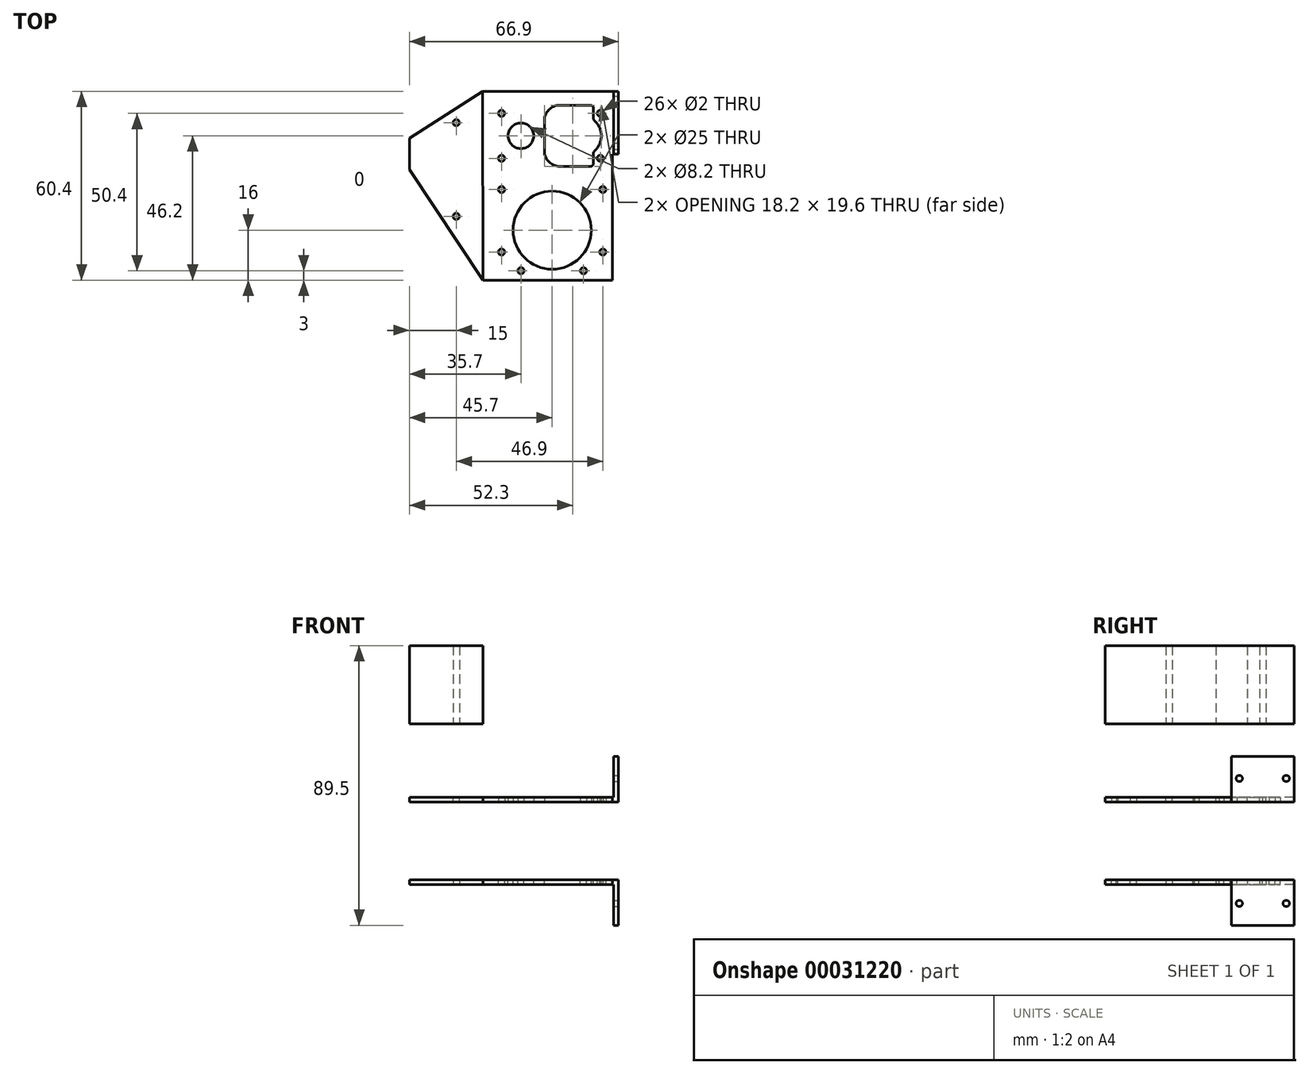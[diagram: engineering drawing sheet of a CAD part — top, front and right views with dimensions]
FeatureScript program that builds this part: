
annotation { "Feature Type Name" : "Feature", "Feature Type Description" : "" }
export const myFeature = defineFeature(function(context is Context, id is Id, definition is map)
    precondition{}
    {
        {
            var Q0;
            Q0=qCreatedBy(makeId("Top.planeOp"),FACE);
            var sketch = newSketch(context, id + "F0", { "sketchPlane" : qUnion([Q0])});
            skLineSegment(sketch, "E0.top", {"start": v(19.2, 14.2) * mm, "end": v(-19.2, 14.2) * mm});
            skLineSegment(sketch, "E0.left", {"start": v(19.2, -14.2) * mm, "end": v(19.2, 14.2) * mm});
            skLineSegment(sketch, "E0.right", {"start": v(-19.2, -14.2) * mm, "end": v(-19.2, 14.2) * mm});
            skPoint(sketch, "E0.middle", {"position": v(0, 0) * mm});
            skCircle(sketch, "E1", {"center": v(-10, 0) * mm, "radius": 4.1 * mm});
            skCircle(sketch, "E2", {"center": v(-16.2, 7.2) * mm, "radius": 1 * mm});
            skCircle(sketch, "E3", {"center": v(15.4, 7.2) * mm, "radius": 1 * mm});
            skLineSegment(sketch, "E4.bottom", {"start": v(2.5, 9.8) * mm, "end": v(12.2, 9.8) * mm});
            skLineSegment(sketch, "E4.top", {"start": v(2.5, -9.8) * mm, "end": v(12.2, -9.8) * mm});
            skLineSegment(sketch, "E4.left", {"start": v(-2.5, 4.8) * mm, "end": v(-2.5, -4.8) * mm});
            skLineSegment(sketch, "E4.right", {"start": v(13.2, 8.8) * mm, "end": v(13.2, 5.6) * mm});
            skPoint(sketch, "E4.middle", {"position": v(5.35, 0) * mm});
            skPoint(sketch, "E5.visualSharp", {"position": v(-2.5, 9.8) * mm});
            skArc(sketch, "E5.filletArc", {"start": v(2.5, 9.8) * mm, "mid": v(-1.04, 8.34) * mm, "end": v(-2.5, 4.8) * mm});
            skPoint(sketch, "E6.visualSharp", {"position": v(-2.5, -9.8) * mm});
            skArc(sketch, "E6.filletArc", {"start": v(-2.5, -4.8) * mm, "mid": v(-1.04, -8.34) * mm, "end": v(2.5, -9.8) * mm});
            skPoint(sketch, "E7.visualSharp", {"position": v(13.2, 9.8) * mm});
            skArc(sketch, "E7.filletArc", {"start": v(13.2, 8.8) * mm, "mid": v(12.9, 9.5) * mm, "end": v(12.2, 9.8) * mm});
            skPoint(sketch, "E8.visualSharp", {"position": v(13.2, -9.8) * mm});
            skArc(sketch, "E8.filletArc", {"start": v(12.2, -9.8) * mm, "mid": v(12.9, -9.5) * mm, "end": v(13.2, -8.8) * mm});
            skCircle(sketch, "E9.MirrorC", {"center": v(-16.2, -7.2) * mm, "radius": 1 * mm});
            skCircle(sketch, "E10.MirrorC", {"center": v(15.4, -7.2) * mm, "radius": 1 * mm});
            skArc(sketch, "E11", {"start": v(13.53, -4.84) * mm, "mid": v(15.7, 0) * mm, "end": v(13.53, 4.84) * mm});
            skLineSegment(sketch, "E12.trimOffspring", {"start": v(13.2, -5.6) * mm, "end": v(13.2, -8.8) * mm});
            skPoint(sketch, "E13.visualSharp", {"position": v(13.2, 5.12) * mm});
            skArc(sketch, "E13.filletArc", {"start": v(13.2, 5.6) * mm, "mid": v(13.29, 5.18) * mm, "end": v(13.53, 4.84) * mm});
            skPoint(sketch, "E14.visualSharp", {"position": v(13.2, -5.12) * mm});
            skArc(sketch, "E14.filletArc", {"start": v(13.53, -4.84) * mm, "mid": v(13.29, -5.18) * mm, "end": v(13.2, -5.6) * mm});
            skLineSegment(sketch, "E15.bottom", {"start": v(-19.2, -14.2) * mm, "end": v(19.2, -14.2) * mm, "construction": true});
            skLineSegment(sketch, "E15.top", {"start": v(-19.2, -46.2) * mm, "end": v(19.2, -46.2) * mm});
            skLineSegment(sketch, "E15.left", {"start": v(-19.2, -14.2) * mm, "end": v(-19.2, -46.2) * mm});
            skLineSegment(sketch, "E15.right", {"start": v(19.2, -14.2) * mm, "end": v(19.2, -46.2) * mm});
            skCircle(sketch, "E16", {"center": v(-10, -43.2) * mm, "radius": 1 * mm});
            skCircle(sketch, "E17.MirrorC", {"center": v(10, -43.2) * mm, "radius": 1 * mm});
            skCircle(sketch, "E18", {"center": v(16.2, -37.2) * mm, "radius": 1 * mm});
            skCircle(sketch, "E19", {"center": v(16.2, -17.2) * mm, "radius": 1 * mm});
            skCircle(sketch, "E20.MirrorC", {"center": v(-16.2, -17.2) * mm, "radius": 1 * mm});
            skCircle(sketch, "E21.MirrorC", {"center": v(-16.2, -37.2) * mm, "radius": 1 * mm});
            skCircle(sketch, "E22", {"center": v(0, -30.2) * mm, "radius": 12.5 * mm});
            skSolve(sketch);
        }
        {
            var Q0;
            Q0=qSketchRegion(id+"F0",true);
            extrude(context, id + "F1", {"entities" : qUnion([Q0]), "depth" : 1.5 * mm});
        }
        {
            var Q0;
            Q0=makeQuery(id+"F1.opExtrude","SWEPT_FACE",FACE,{"disambiguationData":[OSD([sQuery(id+"F0.wireOp",EDGE,"E0.left"),sQuery(id+"F0.wireOp",EDGE,"E15.right")])]});
            var sketch = newSketch(context, id + "F2", { "sketchPlane" : qUnion([Q0])});
            skLineSegment(sketch, "E23.bottom", {"start": v(14.2, 0) * mm, "end": v(-5.8, 0) * mm});
            skLineSegment(sketch, "E23.top", {"start": v(14.2, 1.5) * mm, "end": v(-5.8, 1.5) * mm});
            skLineSegment(sketch, "E23.left", {"start": v(14.2, 0) * mm, "end": v(14.2, 1.5) * mm});
            skLineSegment(sketch, "E23.right", {"start": v(-5.8, 0) * mm, "end": v(-5.8, 1.5) * mm});
            skSolve(sketch);
        }
        {
            var Q0;
            Q0 = qSketchRegion(id + "F2", true);
            extrude(context, id + "F3", {"entities" : qUnion([Q0]), "operationType" : NewBodyOperationType.ADD, "depth" : 2 * mm});
        }
        {
            var Q0;
            Q0=makeQuery(id+"F3.boolean.opBoolean","MERGE",FACE,{"derivedFrom":[makeQuery(id+"F1.opExtrude","CAP_FACE",FACE,{"disambiguationData":[OSD([sQuery(id+"F0.wireOp",EDGE,"E0.top"),sQuery(id+"F0.wireOp",EDGE,"E0.left"),sQuery(id+"F0.wireOp",EDGE,"E0.right"),sQuery(id+"F0.wireOp",EDGE,"E1"),sQuery(id+"F0.wireOp",EDGE,"E2"),sQuery(id+"F0.wireOp",EDGE,"E3"),sQuery(id+"F0.wireOp",EDGE,"E4.bottom"),sQuery(id+"F0.wireOp",EDGE,"E4.top"),sQuery(id+"F0.wireOp",EDGE,"E4.left"),sQuery(id+"F0.wireOp",EDGE,"E4.right"),sQuery(id+"F0.wireOp",EDGE,"E5.filletArc"),sQuery(id+"F0.wireOp",EDGE,"E6.filletArc"),sQuery(id+"F0.wireOp",EDGE,"E7.filletArc"),sQuery(id+"F0.wireOp",EDGE,"E8.filletArc"),sQuery(id+"F0.wireOp",EDGE,"E9.MirrorC"),sQuery(id+"F0.wireOp",EDGE,"E10.MirrorC"),sQuery(id+"F0.wireOp",EDGE,"E11"),sQuery(id+"F0.wireOp",EDGE,"E12.trimOffspring"),sQuery(id+"F0.wireOp",EDGE,"E13.filletArc"),sQuery(id+"F0.wireOp",EDGE,"E14.filletArc"),sQuery(id+"F0.wireOp",EDGE,"E15.top"),sQuery(id+"F0.wireOp",EDGE,"E15.left"),sQuery(id+"F0.wireOp",EDGE,"E15.right"),sQuery(id+"F0.wireOp",EDGE,"E16"),sQuery(id+"F0.wireOp",EDGE,"E17.MirrorC"),sQuery(id+"F0.wireOp",EDGE,"E18"),sQuery(id+"F0.wireOp",EDGE,"E19"),sQuery(id+"F0.wireOp",EDGE,"E20.MirrorC"),sQuery(id+"F0.wireOp",EDGE,"E21.MirrorC")])],"isStart":false}),makeQuery(id+"F3.opExtrude","SWEPT_FACE",FACE,{"disambiguationData":[OSD([sQuery(id+"F2.wireOp",EDGE,"E23.top")])]})]});
            var sketch = newSketch(context, id + "F4", { "sketchPlane" : qUnion([Q0])});
            skLineSegment(sketch, "E24.bottom", {"start": v(19.7, 14.2) * mm, "end": v(21.2, 14.2) * mm});
            skLineSegment(sketch, "E24.top", {"start": v(19.7, -5.8) * mm, "end": v(21.2, -5.8) * mm});
            skLineSegment(sketch, "E24.left", {"start": v(19.7, 14.2) * mm, "end": v(19.7, -5.8) * mm});
            skLineSegment(sketch, "E24.right", {"start": v(21.2, 14.2) * mm, "end": v(21.2, -5.8) * mm});
            skSolve(sketch);
        }
        {
            var Q0;
            Q0 = qSketchRegion(id + "F4", true);
            extrude(context, id + "F5", {"entities" : qUnion([Q0]), "operationType" : NewBodyOperationType.ADD, "depth" : 13 * mm});
        }
        {
            var Q0;
            Q0=qCreatedBy(makeId("Top.planeOp"),FACE);
            cPlane(context, id + "F6", {"entities" : qUnion([Q0]), "cplaneType" : CPlaneType.OFFSET, "offset" : (25 / 2) * mm, "oppositeDirection" : true, "width" : 150 * mm, "height" : 150 * mm});
        }
        {
            var Q0;
            Q0=makeQuery(id+"F1.opExtrude","SWEPT_BODY",BODY,{"disambiguationData":[OSD([sQuery(id+"F0.wireOp",EDGE,"E0.top"),sQuery(id+"F0.wireOp",EDGE,"E0.left"),sQuery(id+"F0.wireOp",EDGE,"E0.right"),sQuery(id+"F0.wireOp",EDGE,"E1"),sQuery(id+"F0.wireOp",EDGE,"E2"),sQuery(id+"F0.wireOp",EDGE,"E3"),sQuery(id+"F0.wireOp",EDGE,"E4.bottom"),sQuery(id+"F0.wireOp",EDGE,"E4.top"),sQuery(id+"F0.wireOp",EDGE,"E4.left"),sQuery(id+"F0.wireOp",EDGE,"E4.right"),sQuery(id+"F0.wireOp",EDGE,"E5.filletArc"),sQuery(id+"F0.wireOp",EDGE,"E6.filletArc"),sQuery(id+"F0.wireOp",EDGE,"E7.filletArc"),sQuery(id+"F0.wireOp",EDGE,"E8.filletArc"),sQuery(id+"F0.wireOp",EDGE,"E9.MirrorC"),sQuery(id+"F0.wireOp",EDGE,"E10.MirrorC"),sQuery(id+"F0.wireOp",EDGE,"E11"),sQuery(id+"F0.wireOp",EDGE,"E12.trimOffspring"),sQuery(id+"F0.wireOp",EDGE,"E13.filletArc"),sQuery(id+"F0.wireOp",EDGE,"E14.filletArc"),sQuery(id+"F0.wireOp",EDGE,"E15.top"),sQuery(id+"F0.wireOp",EDGE,"E15.left"),sQuery(id+"F0.wireOp",EDGE,"E15.right"),sQuery(id+"F0.wireOp",EDGE,"E16"),sQuery(id+"F0.wireOp",EDGE,"E17.MirrorC"),sQuery(id+"F0.wireOp",EDGE,"E18"),sQuery(id+"F0.wireOp",EDGE,"E19"),sQuery(id+"F0.wireOp",EDGE,"E20.MirrorC"),sQuery(id+"F0.wireOp",EDGE,"E21.MirrorC")])]});
            var Q1;
            Q1=qCreatedBy(id+"F6.planeOp",FACE);
            mirror(context, id + "F7", {"entities" : qUnion([Q0]), "mirrorPlane" : qUnion([Q1])});
        }
        {
            var Q0;
            Q0=makeQuery(id+"F7.opPattern","COPY",FACE,{"derivedFrom":makeQuery(id+"F5.boolean.opBoolean","MERGE",FACE,{"derivedFrom":[makeQuery(id+"F3.opExtrude","CAP_FACE",FACE,{"disambiguationData":[OSD([sQuery(id+"F2.wireOp",EDGE,"E23.bottom"),sQuery(id+"F2.wireOp",EDGE,"E23.top"),sQuery(id+"F2.wireOp",EDGE,"E23.left"),sQuery(id+"F2.wireOp",EDGE,"E23.right")])],"isStart":false}),makeQuery(id+"F5.opExtrude","SWEPT_FACE",FACE,{"disambiguationData":[OSD([sQuery(id+"F4.wireOp",EDGE,"E24.right")])]})]}),"instanceName":"1"});
            var sketch = newSketch(context, id + "F8", { "sketchPlane" : qUnion([Q0])});
            skCircle(sketch, "E25", {"center": v(11.7, 7.5) * mm, "radius": 1 * mm});
            skCircle(sketch, "E26", {"center": v(-3.3, 7.5) * mm, "radius": 1 * mm});
            skCircle(sketch, "E27.MirrorC", {"center": v(11.7, -32.5) * mm, "radius": 1 * mm});
            skCircle(sketch, "E28.MirrorC", {"center": v(-3.3, -32.5) * mm, "radius": 1 * mm});
            skSolve(sketch);
        }
        {
            var Q0;
            Q0 = qSketchRegion(id + "F8", true);
            extrude(context, id + "F9", {"entities" : qUnion([Q0]), "operationType" : NewBodyOperationType.REMOVE, "endBound" : BoundingType.UP_TO_NEXT, "oppositeDirection" : true, "depth" : 25 * mm});
        }
        {
            var Q0;
            Q0=makeQuery(id+"F1.opExtrude","SWEPT_FACE",FACE,{"disambiguationData":[OSD([sQuery(id+"F0.wireOp",EDGE,"E0.right"),sQuery(id+"F0.wireOp",EDGE,"E15.left")])]});
            var sketch = newSketch(context, id + "F10", { "sketchPlane" : qUnion([Q0])});
            skLineSegment(sketch, "E29.bottom", {"start": v(-14.2, 0) * mm, "end": v(46.2, 0) * mm});
            skLineSegment(sketch, "E29.top", {"start": v(-14.2, 1.5) * mm, "end": v(46.2, 1.5) * mm});
            skLineSegment(sketch, "E29.left", {"start": v(-14.2, 0) * mm, "end": v(-14.2, 1.5) * mm});
            skLineSegment(sketch, "E29.right", {"start": v(46.2, 0) * mm, "end": v(46.2, 1.5) * mm});
            skSolve(sketch);
        }
        {
            var Q0;
            Q0 = qSketchRegion(id + "F10", true);
            extrude(context, id + "F11", {"entities" : qUnion([Q0]), "operationType" : NewBodyOperationType.ADD, "depth" : (25 + 1.5) * mm});
        }
        {
            var Q0;
            Q0=makeQuery(id+"F11.boolean.opBoolean","MERGE",FACE,{"derivedFrom":[makeQuery(id+"F3.boolean.opBoolean","MERGE",FACE,{"derivedFrom":[makeQuery(id+"F1.opExtrude","CAP_FACE",FACE,{"disambiguationData":[OSD([sQuery(id+"F0.wireOp",EDGE,"E0.top"),sQuery(id+"F0.wireOp",EDGE,"E0.left"),sQuery(id+"F0.wireOp",EDGE,"E0.right"),sQuery(id+"F0.wireOp",EDGE,"E1"),sQuery(id+"F0.wireOp",EDGE,"E2"),sQuery(id+"F0.wireOp",EDGE,"E3"),sQuery(id+"F0.wireOp",EDGE,"E4.bottom"),sQuery(id+"F0.wireOp",EDGE,"E4.top"),sQuery(id+"F0.wireOp",EDGE,"E4.left"),sQuery(id+"F0.wireOp",EDGE,"E4.right"),sQuery(id+"F0.wireOp",EDGE,"E5.filletArc"),sQuery(id+"F0.wireOp",EDGE,"E6.filletArc"),sQuery(id+"F0.wireOp",EDGE,"E7.filletArc"),sQuery(id+"F0.wireOp",EDGE,"E8.filletArc"),sQuery(id+"F0.wireOp",EDGE,"E9.MirrorC"),sQuery(id+"F0.wireOp",EDGE,"E10.MirrorC"),sQuery(id+"F0.wireOp",EDGE,"E11"),sQuery(id+"F0.wireOp",EDGE,"E12.trimOffspring"),sQuery(id+"F0.wireOp",EDGE,"E13.filletArc"),sQuery(id+"F0.wireOp",EDGE,"E14.filletArc"),sQuery(id+"F0.wireOp",EDGE,"E15.top"),sQuery(id+"F0.wireOp",EDGE,"E15.left"),sQuery(id+"F0.wireOp",EDGE,"E15.right"),sQuery(id+"F0.wireOp",EDGE,"E16"),sQuery(id+"F0.wireOp",EDGE,"E17.MirrorC"),sQuery(id+"F0.wireOp",EDGE,"E18"),sQuery(id+"F0.wireOp",EDGE,"E19"),sQuery(id+"F0.wireOp",EDGE,"E20.MirrorC"),sQuery(id+"F0.wireOp",EDGE,"E21.MirrorC")])],"isStart":false}),makeQuery(id+"F3.opExtrude","SWEPT_FACE",FACE,{"disambiguationData":[OSD([sQuery(id+"F2.wireOp",EDGE,"E23.top")])]})]}),makeQuery(id+"F11.opExtrude","SWEPT_FACE",FACE,{"disambiguationData":[OSD([sQuery(id+"F10.wireOp",EDGE,"E29.top")])]})]});
            var sketch = newSketch(context, id + "F12", { "sketchPlane" : qUnion([Q0])});
            skLineSegment(sketch, "E30", {"start": v(-20.7, 14.2) * mm, "end": v(-20.7, -46.2) * mm, "construction": true});
            skLineSegment(sketch, "E31", {"start": v(-22.25, 14.2) * mm, "end": v(-45.7, -0.8) * mm});
            skLineSegment(sketch, "E32", {"start": v(-45.7, -0.8) * mm, "end": v(-45.7, -10.8) * mm});
            skLineSegment(sketch, "E33", {"start": v(-45.7, -10.8) * mm, "end": v(-22.2, -46.2) * mm});
            skLineSegment(sketch, "E34", {"start": v(-22.2, -46.2) * mm, "end": v(-45.7, -46.2) * mm});
            skLineSegment(sketch, "E35", {"start": v(-45.7, -46.2) * mm, "end": v(-45.7, -10.8) * mm});
            skLineSegment(sketch, "E36", {"start": v(-22.25, 14.2) * mm, "end": v(-45.7, 14.2) * mm});
            skLineSegment(sketch, "E37", {"start": v(-45.7, 14.2) * mm, "end": v(-45.7, -0.8) * mm});
            skCircle(sketch, "E38", {"center": v(-30.7, 4.2) * mm, "radius": 1 * mm});
            skCircle(sketch, "E39", {"center": v(-30.7, -25.8) * mm, "radius": 1 * mm});
            skLineSegment(sketch, "E40", {"start": v(-30.7, 4.2) * mm, "end": v(-30.7, -25.8) * mm, "construction": true});
            skSolve(sketch);
        }
        {
            var Q0;
            Q0 = qSketchRegion(id + "F12", true);
            extrude(context, id + "F13", {"entities" : qUnion([Q0]), "operationType" : NewBodyOperationType.REMOVE, "endBound" : BoundingType.UP_TO_NEXT, "oppositeDirection" : true, "depth" : 25 * mm});
        }
        {
            var Q0;
            Q0=makeQuery(id+"F1.opExtrude","SWEPT_BODY",BODY,{"disambiguationData":[OSD([sQuery(id+"F0.wireOp",EDGE,"E0.top"),sQuery(id+"F0.wireOp",EDGE,"E0.left"),sQuery(id+"F0.wireOp",EDGE,"E0.right"),sQuery(id+"F0.wireOp",EDGE,"E1"),sQuery(id+"F0.wireOp",EDGE,"E2"),sQuery(id+"F0.wireOp",EDGE,"E3"),sQuery(id+"F0.wireOp",EDGE,"E4.bottom"),sQuery(id+"F0.wireOp",EDGE,"E4.top"),sQuery(id+"F0.wireOp",EDGE,"E4.left"),sQuery(id+"F0.wireOp",EDGE,"E4.right"),sQuery(id+"F0.wireOp",EDGE,"E5.filletArc"),sQuery(id+"F0.wireOp",EDGE,"E6.filletArc"),sQuery(id+"F0.wireOp",EDGE,"E7.filletArc"),sQuery(id+"F0.wireOp",EDGE,"E8.filletArc"),sQuery(id+"F0.wireOp",EDGE,"E9.MirrorC"),sQuery(id+"F0.wireOp",EDGE,"E10.MirrorC"),sQuery(id+"F0.wireOp",EDGE,"E11"),sQuery(id+"F0.wireOp",EDGE,"E12.trimOffspring"),sQuery(id+"F0.wireOp",EDGE,"E13.filletArc"),sQuery(id+"F0.wireOp",EDGE,"E14.filletArc"),sQuery(id+"F0.wireOp",EDGE,"E15.top"),sQuery(id+"F0.wireOp",EDGE,"E15.left"),sQuery(id+"F0.wireOp",EDGE,"E15.right"),sQuery(id+"F0.wireOp",EDGE,"E16"),sQuery(id+"F0.wireOp",EDGE,"E17.MirrorC"),sQuery(id+"F0.wireOp",EDGE,"E18"),sQuery(id+"F0.wireOp",EDGE,"E19"),sQuery(id+"F0.wireOp",EDGE,"E20.MirrorC"),sQuery(id+"F0.wireOp",EDGE,"E21.MirrorC")])]});
            var Q1;
            Q1=qCreatedBy(id+"F6.planeOp",FACE);
            mirror(context, id + "F14", {"operationType" : NewBodyOperationType.ADD, "entities" : qUnion([Q0]), "mirrorPlane" : qUnion([Q1])});
        }
        {
            var Q0;
            Q0=qCreatedBy(makeId("Top.planeOp"),FACE);
            cPlane(context, id + "F15", {"entities" : qUnion([Q0]), "cplaneType" : CPlaneType.OFFSET, "offset" : 25 * mm, "width" : 150 * mm, "height" : 150 * mm});
        }
        {
            var Q0;
            Q0=qCreatedBy(id+"F15.planeOp",FACE);
            var sketch = newSketch(context, id + "F16", { "sketchPlane" : qUnion([Q0])});
            skLineSegment(sketch, "E41.0.0", {"start": v(19.7, 14.2) * mm, "end": v(-22.25, 14.2) * mm, "construction": true});
            skLineSegment(sketch, "E41.0.1", {"start": v(-22.25, 14.2) * mm, "end": v(-45.7, -0.8) * mm});
            skLineSegment(sketch, "E41.0.2", {"start": v(-45.7, -0.8) * mm, "end": v(-45.7, -10.8) * mm});
            skLineSegment(sketch, "E41.0.3", {"start": v(-45.7, -10.8) * mm, "end": v(-22.2, -46.2) * mm});
            skLineSegment(sketch, "E41.0.4", {"start": v(-22.2, -46.2) * mm, "end": v(19.2, -46.2) * mm, "construction": true});
            skLineSegment(sketch, "E41.0.5", {"start": v(19.2, -46.2) * mm, "end": v(19.2, -5.8) * mm, "construction": true});
            skLineSegment(sketch, "E41.0.6", {"start": v(19.2, -5.8) * mm, "end": v(19.7, -5.8) * mm, "construction": true});
            skLineSegment(sketch, "E41.0.7", {"start": v(19.7, -5.8) * mm, "end": v(19.7, 14.2) * mm, "construction": true});
            skLineSegment(sketch, "E42", {"start": v(-22.25, 14.2) * mm, "end": v(-22.2, -46.2) * mm});
            skCircle(sketch, "E43.0", {"center": v(-30.7, 4.2) * mm, "radius": 1 * mm});
            skCircle(sketch, "E43.1", {"center": v(-30.7, -25.8) * mm, "radius": 1 * mm});
            skCircle(sketch, "E43.2", {"center": v(-30.7, 4.2) * mm, "radius": 1 * mm});
            skCircle(sketch, "E43.3", {"center": v(-30.7, -25.8) * mm, "radius": 1 * mm});
            skCircle(sketch, "E43.4", {"center": v(-30.7, 4.2) * mm, "radius": 1 * mm});
            skCircle(sketch, "E43.5", {"center": v(-30.7, -25.8) * mm, "radius": 1 * mm});
            skCircle(sketch, "E43.6", {"center": v(-30.7, -25.8) * mm, "radius": 1 * mm});
            skCircle(sketch, "E43.7", {"center": v(-30.7, 4.2) * mm, "radius": 1 * mm});
            skSolve(sketch);
        }
        {
            var Q0;
            Q0 = qSketchRegion(id + "F16", true);
            extrude(context, id + "F17", {"entities" : qUnion([Q0]), "depth" : 25 * mm});
        }
    });
